# Revit family: S-tank_AT_Prestige
name_source: partatom
category: Оборудование
units: mm (PartAtom-declared; Revit-internal decimal feet)

## family parameters
Всегда вертикально = Да
Классификация = Нет
На основе рабочей плоскости = Нет
Общий = Нет
При загрузке вырезать с полостями = Нет
Размер круглого соединителя = Использовать диаметр
Тип детали = Нормальный
Точка расчета площади = Нет

## types (9) — shared parameters
ADSK_URL документации изделия = http://s-tank.ru
ADSK_Группирование = Оборудование
ADSK_Единица измерения = шт.
ADSK_Завод-изготовитель = ООО “С-ТЭНК ВОТЕР ХИТЕРС”
ADSK_Наименование = Буферная емкость
ADSK_Обозначение = AT300Prestige
DN1 = 40 мм
DN2 = 15 мм
shrf = 18 мм
Разработка семейств = https://rubim.tech

## per-type parameters (varying)
| type | A | ADSK_Марка | ADSK_Масса | B | C | D | E | H | I | K | L | M | a | Диаметрсизоляцией |
| AT300 Prestige | 125 мм | AT 300 Prestige | 65 | 225 мм | 385 мм | 545 мм | 705 мм | 1600 мм | 865 мм | 1025 мм | 1185 мм | 1345 мм | 105 мм | 630 мм |
| AT500 Prestige | 122 мм | AT 500 Prestige | 87 | 220 мм | 380 мм | 540 мм | 700 мм | 1605 мм | 860 мм | 1020 мм | 1180 мм | 1340 мм | 130 мм | 780 мм |
| AT750 Prestige | 117 мм | AT 750 Prestige | 103 | 210 мм | 370 мм | 530 мм | 690 мм | 1630 мм | 850 мм | 1010 мм | 1170 мм | 1330 мм | 153 мм | 920 мм |
| AT1000 Prestige | 117 мм | AT 1000 Prestige | 131 | 200 мм | 445 мм | 680 мм | 935 мм | 2205 мм | 1180 мм | 1425 мм | 1670 мм | 1915 мм | 153 мм | 920 мм |
| AT1200 Prestige | 177 мм | AT 1200 Prestige | 174 | 300 мм | 490 мм | 680 мм | 870 мм | 2080 мм | 1060 мм | 1250 мм | 1440 мм | 1630 мм | 178 мм | 1070 мм |
| AT1500 Prestige | 177 мм | AT 1500 Prestige | 200 | 300 мм | 540 мм | 780 мм | 1020 мм | 2370 мм | 1260 мм | 1500 мм | 1740 мм | 1980 мм | 178 мм | 1070 мм |
| AT2000 Prestige | 250 мм | AT 2000 Prestige | 246 | 385 мм | 575 мм | 765 мм | 955 мм | 2100 мм | 1145 мм | 1335 мм | 1525 мм | 1715 мм | 225 мм | 1350 мм |
| AT3000 Prestige | 332 мм | AT 3000 Prestige | 450 | 500 мм | 690 мм | 880 мм | 1070 мм | 2315 мм | 1260 мм | 1450 мм | 1640 мм | 1830 мм | 272 мм | 1630 мм |
| AT5000 Prestige | 332 мм | AT 5000 Prestige | 615 | 500 мм | 800 мм | 1100 мм | 1400 мм | 2315 мм | 1700 мм | 2000 мм | 2300 мм | 2600 мм | 272 мм | 1630 мм |
